# Revit family: 207_Ross-tuuletuspaalu _
name_source: partatom
category: Air Terminals
units: mm (PartAtom-declared; Revit-internal decimal feet)

## family parameters
Always vertical = Yes
Cut with Voids When Loaded = No
Part Type = Normal
Room Calculation Point = Yes
Round Connector Dimension = Use Diameter
Shared = No
Work Plane-Based = No

## types (3) — shared parameters
CAT0 = Yes
CL_Location_5000 = 5000 mm  [stored 16.4042 ft]
Description = Ross renovation pole
ET = 2 mm  [stored 0.00656168 ft]
L_ARR = 400 mm  [stored 1.31234 ft]
Manufacturer = Vilpe
QmdConnectorList = 201;D
URL = http://www.vilpe.com
W_ARR = 400 mm  [stored 1.31234 ft]
XRefLineVPlnId = 7453
YRefLineVPlnId = 7456
magiPartTypeId = 207
magiProductFamilyId = Ross-tuuletuspaalu *
zero-valued in all types: CLBTZ, H_ARR

## per-type parameters (varying)
| type | CT | D | D1 | D12 | D122 | D13 | D14 | D22 | HC | R1 | magiProductId |
| VILPE ROSS VENTILATION POLE Ø125/135 | 50 mm  [stored 0.164042 ft] | 125 mm | 132 mm  [stored 0.433071 ft] | 70 mm  [stored 0.229659 ft] | 66 mm  [stored 0.216535 ft] | 33 mm  [stored 0.108268 ft] | 136 mm  [stored 0.446194 ft] | 75 mm  [stored 0.246063 ft] | 947 mm  [stored 3.10696 ft] | 105 mm  [stored 0.344488 ft] | Ross-tuuletuspaalu 125/135 |
| VILPE ROSS VENTILATION POLE Ø200/210 | 34 mm | 200 mm | 220 mm | 114 mm | 110 mm | 55 mm | 224 mm | 124 mm | 1237 mm | 65 mm | Ross-tuuletuspaalu 200/210 |
| VILPE ROSS VENTILATION POLE Ø160/170 | 62 mm | 160 mm | 168 mm | 88 mm | 84 mm | 42 mm  [stored 0.137795 ft] | 172 mm | 95 mm | 942 mm | 114 mm | Ross-tuuletuspaalu 160/170 |

note: column(s) folded — value = type name in every type: MC Product Code

note: [stored X ft] marks values corroborated as IEEE doubles in the binary element streams (Revit-internal decimal feet)

## geometry (parser evidence)
native form markers: Sweep x2
no freeform markers — native parametric forms only
